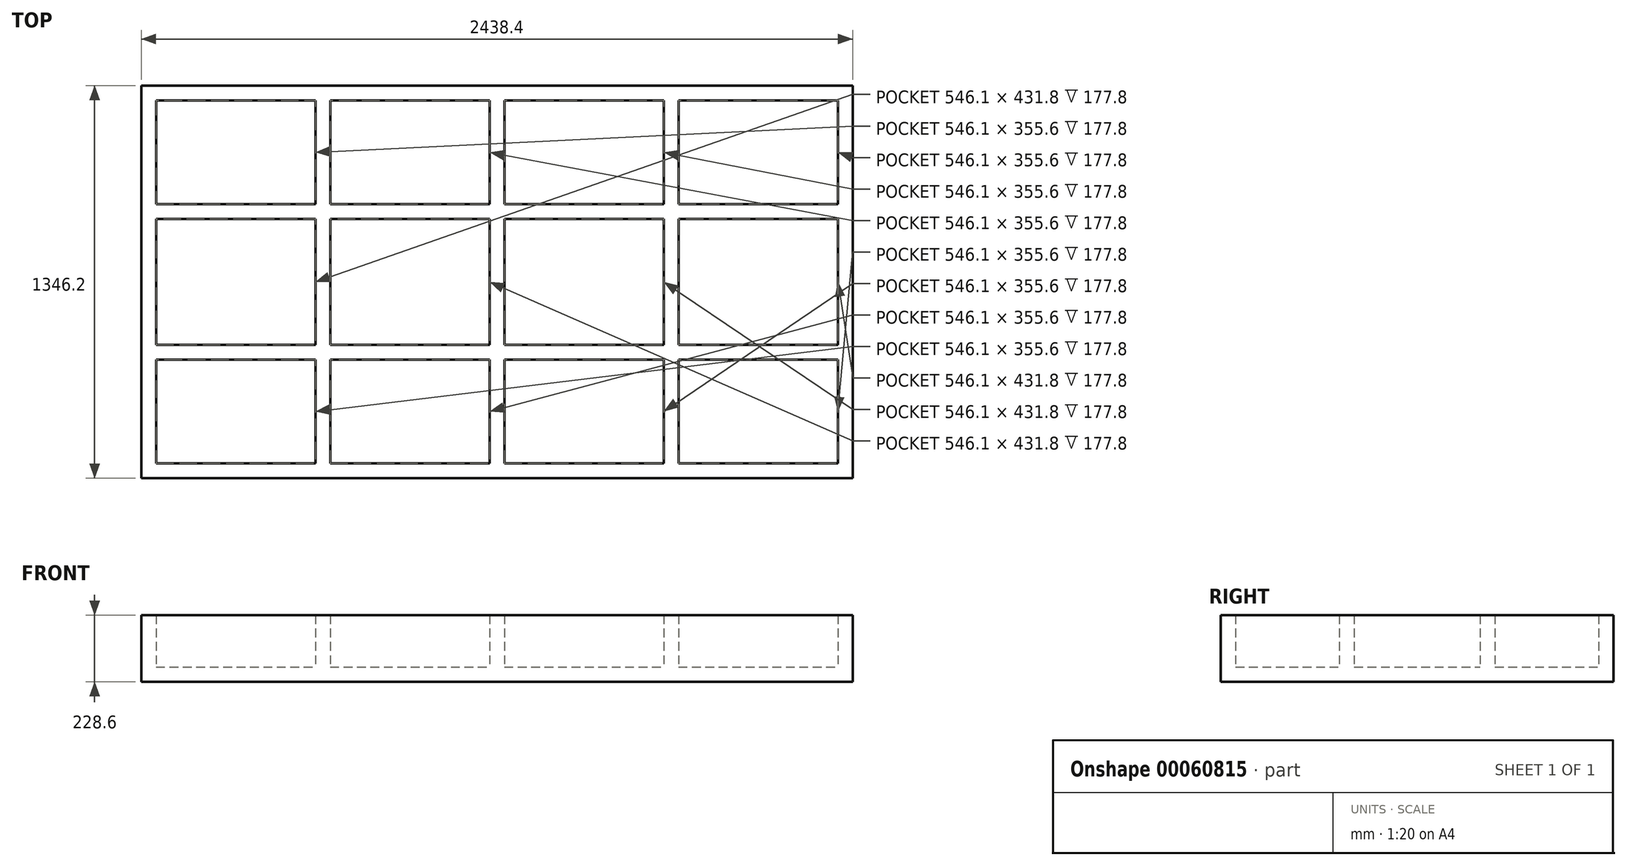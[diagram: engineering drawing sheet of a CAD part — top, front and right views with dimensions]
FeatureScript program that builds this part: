
annotation { "Feature Type Name" : "Feature", "Feature Type Description" : "" }
export const myFeature = defineFeature(function(context is Context, id is Id, definition is map)
    precondition{}
    {
        {
            var Q0;
            Q0=qCreatedBy(makeId("Top.planeOp"),FACE);
            var sketch = newSketch(context, id + "F0", { "sketchPlane" : qUnion([Q0])});
            skLineSegment(sketch, "E0.bottom", {"start": v(-1219.2, 0) * mm, "end": v(1219.2, 0) * mm});
            skLineSegment(sketch, "E0.top", {"start": v(-1219.2, 1346.2) * mm, "end": v(1219.2, 1346.2) * mm});
            skLineSegment(sketch, "E0.left", {"start": v(-1219.2, 0) * mm, "end": v(-1219.2, 1346.2) * mm});
            skLineSegment(sketch, "E0.right", {"start": v(1219.2, 0) * mm, "end": v(1219.2, 1346.2) * mm});
            skSolve(sketch);
        }
        {
            var Q0;
            Q0=makeQuery(id+"F0.imprint","IMPRINT",FACE,{"disambiguationData":[TD([[makeQuery(id+"F0.imprint","IMPRINT",EDGE,{"derivedFrom":sQuery(id+"F0.wireOp",EDGE,"E0.bottom")}),1.0]])]});
            extrude(context, id + "F1", {"entities" : qUnion([Q0]), "depth" : 50.8 * mm});
        }
        {
            var Q0;
            Q0=makeQuery(id+"F1.opExtrude","CAP_FACE",FACE,{"disambiguationData":[OSD([sQuery(id+"F0.wireOp",EDGE,"E0.bottom"),sQuery(id+"F0.wireOp",EDGE,"E0.top"),sQuery(id+"F0.wireOp",EDGE,"E0.left"),sQuery(id+"F0.wireOp",EDGE,"E0.right")])],"isStart":false});
            var sketch = newSketch(context, id + "F2", { "sketchPlane" : qUnion([Q0])});
            skLineSegment(sketch, "E1", {"start": v(-1168.4, 406.4) * mm, "end": v(-622.3, 406.4) * mm});
            skLineSegment(sketch, "E2", {"start": v(-1168.4, 457.2) * mm, "end": v(-622.3, 457.2) * mm});
            skLineSegment(sketch, "E3", {"start": v(-1219.2, 406.4) * mm, "end": v(-1219.2, 457.2) * mm});
            skLineSegment(sketch, "E4", {"start": v(1219.2, 406.4) * mm, "end": v(1219.2, 457.2) * mm});
            skLineSegment(sketch, "E5.bottom", {"start": v(-1168.4, 889) * mm, "end": v(-622.3, 889) * mm});
            skLineSegment(sketch, "E5.top", {"start": v(-1168.4, 939.8) * mm, "end": v(-622.3, 939.8) * mm});
            skLineSegment(sketch, "E5.left", {"start": v(-1219.2, 889) * mm, "end": v(-1219.2, 939.8) * mm});
            skLineSegment(sketch, "E5.right", {"start": v(1219.2, 889) * mm, "end": v(1219.2, 939.8) * mm});
            skLineSegment(sketch, "E6.bottom", {"start": v(-622.3, 0) * mm, "end": v(-571.5, 0) * mm});
            skLineSegment(sketch, "E6.top", {"start": v(-622.3, 1346.2) * mm, "end": v(-571.5, 1346.2) * mm});
            skLineSegment(sketch, "E6.left", {"start": v(-622.3, 50.8) * mm, "end": v(-622.3, 406.4) * mm});
            skLineSegment(sketch, "E6.right", {"start": v(-571.5, 50.8) * mm, "end": v(-571.5, 406.4) * mm});
            skLineSegment(sketch, "E7.bottom", {"start": v(-25.4, 0) * mm, "end": v(25.4, 0) * mm});
            skLineSegment(sketch, "E7.top", {"start": v(-25.4, 1346.2) * mm, "end": v(25.4, 1346.2) * mm});
            skLineSegment(sketch, "E7.left", {"start": v(-25.4, 50.8) * mm, "end": v(-25.4, 406.4) * mm});
            skLineSegment(sketch, "E7.right", {"start": v(25.4, 50.8) * mm, "end": v(25.4, 406.4) * mm});
            skLineSegment(sketch, "E8.bottom", {"start": v(622.3, 0) * mm, "end": v(571.5, 0) * mm});
            skLineSegment(sketch, "E8.top", {"start": v(622.3, 1346.2) * mm, "end": v(571.5, 1346.2) * mm});
            skLineSegment(sketch, "E8.left", {"start": v(622.3, 50.8) * mm, "end": v(622.3, 406.4) * mm});
            skLineSegment(sketch, "E8.right", {"start": v(571.5, 50.8) * mm, "end": v(571.5, 406.4) * mm});
            skLineSegment(sketch, "E9.bottom", {"start": v(1219.2, 0) * mm, "end": v(1168.4, 0) * mm});
            skLineSegment(sketch, "E9.top", {"start": v(1219.2, 1346.2) * mm, "end": v(1168.4, 1346.2) * mm});
            skLineSegment(sketch, "E9.left", {"start": v(1219.2, 0) * mm, "end": v(1219.2, 1346.2) * mm});
            skLineSegment(sketch, "E9.right", {"start": v(1168.4, 50.8) * mm, "end": v(1168.4, 406.4) * mm});
            skLineSegment(sketch, "E10.bottom", {"start": v(-1219.2, 0) * mm, "end": v(-1168.4, 0) * mm});
            skLineSegment(sketch, "E10.top", {"start": v(-1219.2, 1346.2) * mm, "end": v(-1168.4, 1346.2) * mm});
            skLineSegment(sketch, "E10.left", {"start": v(-1219.2, 0) * mm, "end": v(-1219.2, 1346.2) * mm});
            skLineSegment(sketch, "E10.right", {"start": v(-1168.4, 50.8) * mm, "end": v(-1168.4, 406.4) * mm});
            skLineSegment(sketch, "E11.trimOffspring", {"start": v(-1168.4, 457.2) * mm, "end": v(-1168.4, 889) * mm});
            skLineSegment(sketch, "E12.trimOffspring", {"start": v(-1168.4, 939.8) * mm, "end": v(-1168.4, 1295.4) * mm});
            skLineSegment(sketch, "E13.trimOffspring", {"start": v(-622.3, 939.8) * mm, "end": v(-622.3, 1295.4) * mm});
            skLineSegment(sketch, "E14.trimOffspring", {"start": v(-571.5, 889) * mm, "end": v(-25.4, 889) * mm});
            skLineSegment(sketch, "E15.trimOffspring", {"start": v(-571.5, 939.8) * mm, "end": v(-571.5, 1295.4) * mm});
            skLineSegment(sketch, "E16.trimOffspring", {"start": v(-571.5, 939.8) * mm, "end": v(-25.4, 939.8) * mm});
            skLineSegment(sketch, "E17.trimOffspring", {"start": v(-571.5, 457.2) * mm, "end": v(-25.4, 457.2) * mm});
            skLineSegment(sketch, "E18.trimOffspring", {"start": v(-622.3, 457.2) * mm, "end": v(-622.3, 889) * mm});
            skLineSegment(sketch, "E19.trimOffspring", {"start": v(-571.5, 406.4) * mm, "end": v(-25.4, 406.4) * mm});
            skLineSegment(sketch, "E20.trimOffspring", {"start": v(-571.5, 457.2) * mm, "end": v(-571.5, 889) * mm});
            skLineSegment(sketch, "E21.trimOffspring", {"start": v(-25.4, 457.2) * mm, "end": v(-25.4, 889) * mm});
            skLineSegment(sketch, "E22.trimOffspring", {"start": v(25.4, 406.4) * mm, "end": v(571.5, 406.4) * mm});
            skLineSegment(sketch, "E23.trimOffspring", {"start": v(25.4, 457.2) * mm, "end": v(25.4, 889) * mm});
            skLineSegment(sketch, "E24.trimOffspring", {"start": v(25.4, 457.2) * mm, "end": v(571.5, 457.2) * mm});
            skLineSegment(sketch, "E25.trimOffspring", {"start": v(25.4, 889) * mm, "end": v(571.5, 889) * mm});
            skLineSegment(sketch, "E26.trimOffspring", {"start": v(-25.4, 939.8) * mm, "end": v(-25.4, 1295.4) * mm});
            skLineSegment(sketch, "E27.trimOffspring", {"start": v(25.4, 939.8) * mm, "end": v(571.5, 939.8) * mm});
            skLineSegment(sketch, "E28.trimOffspring", {"start": v(25.4, 939.8) * mm, "end": v(25.4, 1295.4) * mm});
            skLineSegment(sketch, "E29.trimOffspring", {"start": v(571.5, 457.2) * mm, "end": v(571.5, 889) * mm});
            skLineSegment(sketch, "E30.trimOffspring", {"start": v(622.3, 406.4) * mm, "end": v(1168.4, 406.4) * mm});
            skLineSegment(sketch, "E31.trimOffspring", {"start": v(622.3, 457.2) * mm, "end": v(622.3, 889) * mm});
            skLineSegment(sketch, "E32.trimOffspring", {"start": v(622.3, 457.2) * mm, "end": v(1168.4, 457.2) * mm});
            skLineSegment(sketch, "E33.trimOffspring", {"start": v(622.3, 889) * mm, "end": v(1168.4, 889) * mm});
            skLineSegment(sketch, "E34.trimOffspring", {"start": v(571.5, 939.8) * mm, "end": v(571.5, 1295.4) * mm});
            skLineSegment(sketch, "E35.trimOffspring", {"start": v(622.3, 939.8) * mm, "end": v(1168.4, 939.8) * mm});
            skLineSegment(sketch, "E36.trimOffspring", {"start": v(622.3, 939.8) * mm, "end": v(622.3, 1295.4) * mm});
            skLineSegment(sketch, "E37.trimOffspring", {"start": v(1168.4, 939.8) * mm, "end": v(1168.4, 1295.4) * mm});
            skLineSegment(sketch, "E38.trimOffspring", {"start": v(1168.4, 457.2) * mm, "end": v(1168.4, 889) * mm});
            skLineSegment(sketch, "E39.bottom", {"start": v(-1219.2, 0) * mm, "end": v(1219.2, 0) * mm});
            skLineSegment(sketch, "E39.top", {"start": v(-1168.4, 50.8) * mm, "end": v(-622.3, 50.8) * mm});
            skLineSegment(sketch, "E39.left", {"start": v(-1219.2, 0) * mm, "end": v(-1219.2, 50.8) * mm});
            skLineSegment(sketch, "E39.right", {"start": v(1219.2, 0) * mm, "end": v(1219.2, 50.8) * mm});
            skLineSegment(sketch, "E40.bottom", {"start": v(-1219.2, 1346.2) * mm, "end": v(1219.2, 1346.2) * mm});
            skLineSegment(sketch, "E40.top", {"start": v(-1168.4, 1295.4) * mm, "end": v(-622.3, 1295.4) * mm});
            skLineSegment(sketch, "E40.left", {"start": v(-1219.2, 1346.2) * mm, "end": v(-1219.2, 1295.4) * mm});
            skLineSegment(sketch, "E40.right", {"start": v(1219.2, 1346.2) * mm, "end": v(1219.2, 1295.4) * mm});
            skLineSegment(sketch, "E41.trimOffspring", {"start": v(-571.5, 50.8) * mm, "end": v(-25.4, 50.8) * mm});
            skLineSegment(sketch, "E42.trimOffspring", {"start": v(25.4, 50.8) * mm, "end": v(571.5, 50.8) * mm});
            skLineSegment(sketch, "E43.trimOffspring", {"start": v(622.3, 50.8) * mm, "end": v(1168.4, 50.8) * mm});
            skLineSegment(sketch, "E44.trimOffspring", {"start": v(622.3, 1295.4) * mm, "end": v(1168.4, 1295.4) * mm});
            skLineSegment(sketch, "E45.trimOffspring", {"start": v(25.4, 1295.4) * mm, "end": v(571.5, 1295.4) * mm});
            skLineSegment(sketch, "E46.trimOffspring", {"start": v(-571.5, 1295.4) * mm, "end": v(-25.4, 1295.4) * mm});
            skSolve(sketch);
        }
        {
            var Q0;
            Q0 = qSketchRegion(id + "F2", true);
            extrude(context, id + "F3", {"entities" : qUnion([Q0]), "operationType" : NewBodyOperationType.ADD, "depth" : 177.8 * mm});
        }
    });
